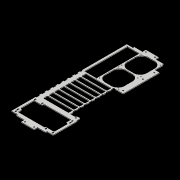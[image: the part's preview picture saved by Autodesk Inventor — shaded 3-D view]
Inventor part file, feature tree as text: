
AUTODESK INVENTOR PART (.ipt)
format: ipt  version: 2018.2 (Build 222227000, 227)  size: 951,296 bytes
history: native  units: mm
features: reference x43, extrude x18, sketch x18, other x14, fillet x6
ambient origin geometry x8: Origin, YZ Plane, XZ Plane, XY Plane, X Axis, Y Axis, Z Axis, Center Point
bodies: Body1 (feature_tree)
feature tree (99):
  other  "ソリッド1"
  extrude  "押し出し1"  Depth=110.0mm
  extrude  "押し出し2"  Depth=430.0mm
  extrude  "押し出し3"  Depth=17.5mm
  extrude  "押し出し4"  Depth=17.5mm
  extrude  "押し出し5"  Depth=20.0mm
  fillet  "フィレット1"  Radius=20.0mm
  extrude  "押し出し6"  Depth=10.0mm
  extrude  "押し出し7"  Depth=10.0mm
  extrude  "押し出し8"  Depth=10.0mm
  fillet  "フィレット3"  Radius=10.0mm
  extrude  "押し出し9"  Depth=4.5mm
  extrude  "押し出し10"  Depth=10.0mm
  extrude  "押し出し11"  Depth=10.0mm
  extrude  "押し出し12"  Depth=3.0mm TaperAngle=0.0deg
  extrude  "押し出し13"  Depth=44.7mm
  extrude  "押し出し14"  Depth=159.0mm
  extrude  "押し出し15"  Depth=3.0mm TaperAngle=0.0deg
  extrude  "押し出し16"  Depth=3.0mm
  fillet  "フィレット4"  Radius=3.0mm
  extrude  "押し出し17"  Depth=3.0mm TaperAngle=0.0deg
  fillet  "フィレット5"  Radius=8.06mm
  fillet  "フィレット6"  Radius=93.68mm
  extrude  "押し出し18"  Depth=15.88mm
  fillet  "フィレット7"  Radius=9.53mm
  sketch  "スケッチ1"
  sketch  "スケッチ2"
  reference  "参照1"
  reference  "参照2"
  reference  "参照3"
  reference  "参照4"
  sketch  "スケッチ3"
  reference  "参照5"
  reference  "参照6"
  reference  "参照7"
  reference  "参照8"
  reference  "参照9"
  reference  "参照10"
  reference  "参照11"
  reference  "参照12"
  reference  "参照13"
  reference  "参照14"
  reference  "参照15"
  reference  "参照16"
  reference  "参照17"
  reference  "参照18"
  reference  "参照19"
  reference  "参照20"
  sketch  "スケッチ4"
  reference  "参照21"
  reference  "参照22"
  reference  "参照23"
  reference  "参照24"
  sketch  "スケッチ5"
  reference  "参照25"
  reference  "参照26"
  reference  "参照27"
  reference  "参照28"
  reference  "参照29"
  reference  "参照30"
  reference  "参照31"
  reference  "参照32"
  sketch  "スケッチ6"
  sketch  "スケッチ7"
  sketch  "スケッチ8"
  sketch  "スケッチ9"
  reference  "参照33"
  reference  "参照34"
  reference  "参照35"
  reference  "参照36"
  reference  "参照37"
  reference  "参照38"
  reference  "参照39"
  reference  "参照40"
  reference  "参照41"
  reference  "参照42"
  reference  "参照43"
  sketch  "スケッチ10"
  sketch  "スケッチ11"
  sketch  "スケッチ12"
  sketch  "スケッチ13"
  sketch  "スケッチ14"
  sketch  "スケッチ15"
  sketch  "スケッチ16"
  sketch  "スケッチ17"
  sketch  "スケッチ18"
  other  "<userpath>\Documents\CAD\eatx_case\layout.iam"
  other  "layout.iam"
  other  "Rampage V Extreme Assembly:1"
  other  "R5E io shield_101"
  other  "titan assembly:3"
  other  "titan dual bracket:1"
  other  "titan assembly:4"
  other  "titan assembly:2"
  other  "titan assembly:1"
  other  "Rampage V Extreme PCB_1"
  other  "ATX Power Supply v1.0:1"
  other  "Box v1.0 - ATX Power Supply"
  other  "Cover v1.0 - ATX Power Supply"
